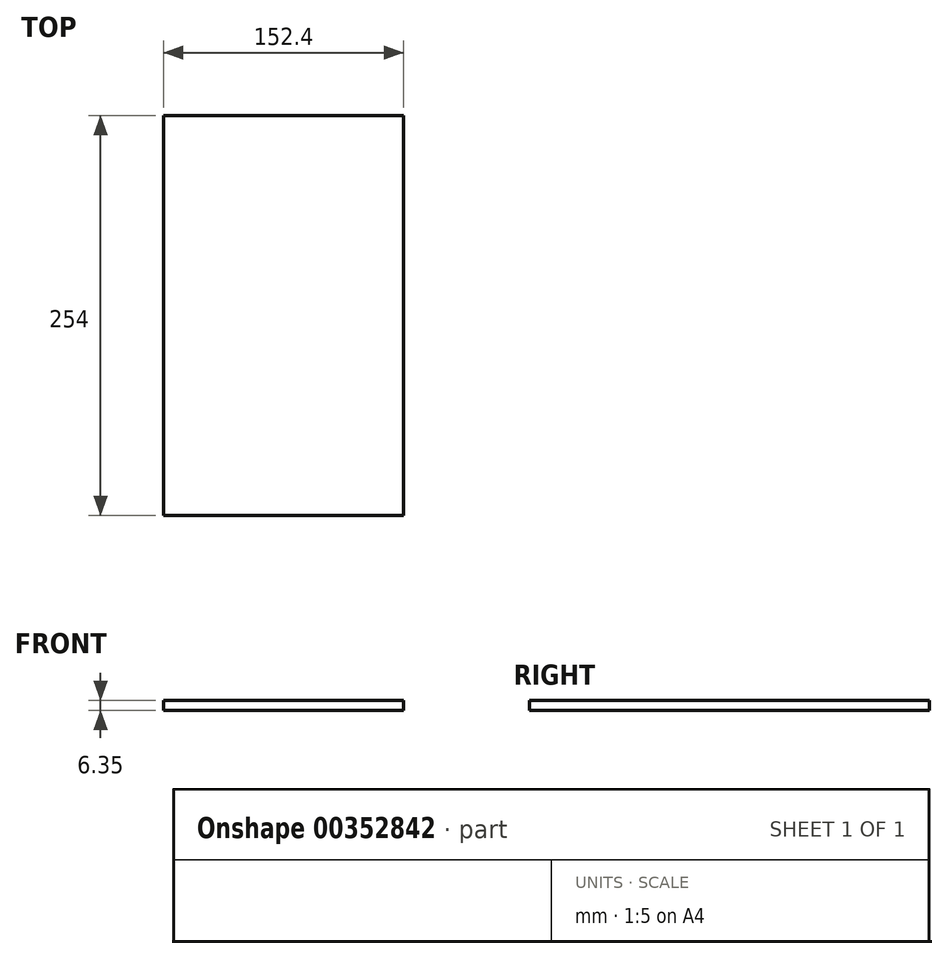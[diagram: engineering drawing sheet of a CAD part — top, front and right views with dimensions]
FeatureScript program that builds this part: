
annotation { "Feature Type Name" : "Feature", "Feature Type Description" : "" }
export const myFeature = defineFeature(function(context is Context, id is Id, definition is map)
    precondition{}
    {
        {
            var Q0;
            Q0=qCreatedBy(makeId("Top.planeOp"),FACE);
            var sketch = newSketch(context, id + "F0", { "sketchPlane" : qUnion([Q0])});
            skLineSegment(sketch, "E0.bottom", {"start": v(76.2, 127) * mm, "end": v(-76.2, 127) * mm});
            skLineSegment(sketch, "E0.top", {"start": v(76.2, -127) * mm, "end": v(-76.2, -127) * mm});
            skLineSegment(sketch, "E0.left", {"start": v(76.2, 127) * mm, "end": v(76.2, -127) * mm});
            skLineSegment(sketch, "E0.right", {"start": v(-76.2, 127) * mm, "end": v(-76.2, -127) * mm});
            skPoint(sketch, "E0.middle", {"position": v(0, 0) * mm});
            skSolve(sketch);
        }
        {
            var Q0;
            Q0 = qSketchRegion(id + "F0", true);
            extrude(context, id + "F1", {"entities" : qUnion([Q0]), "depth" : 6.35 * mm});
        }
    });
